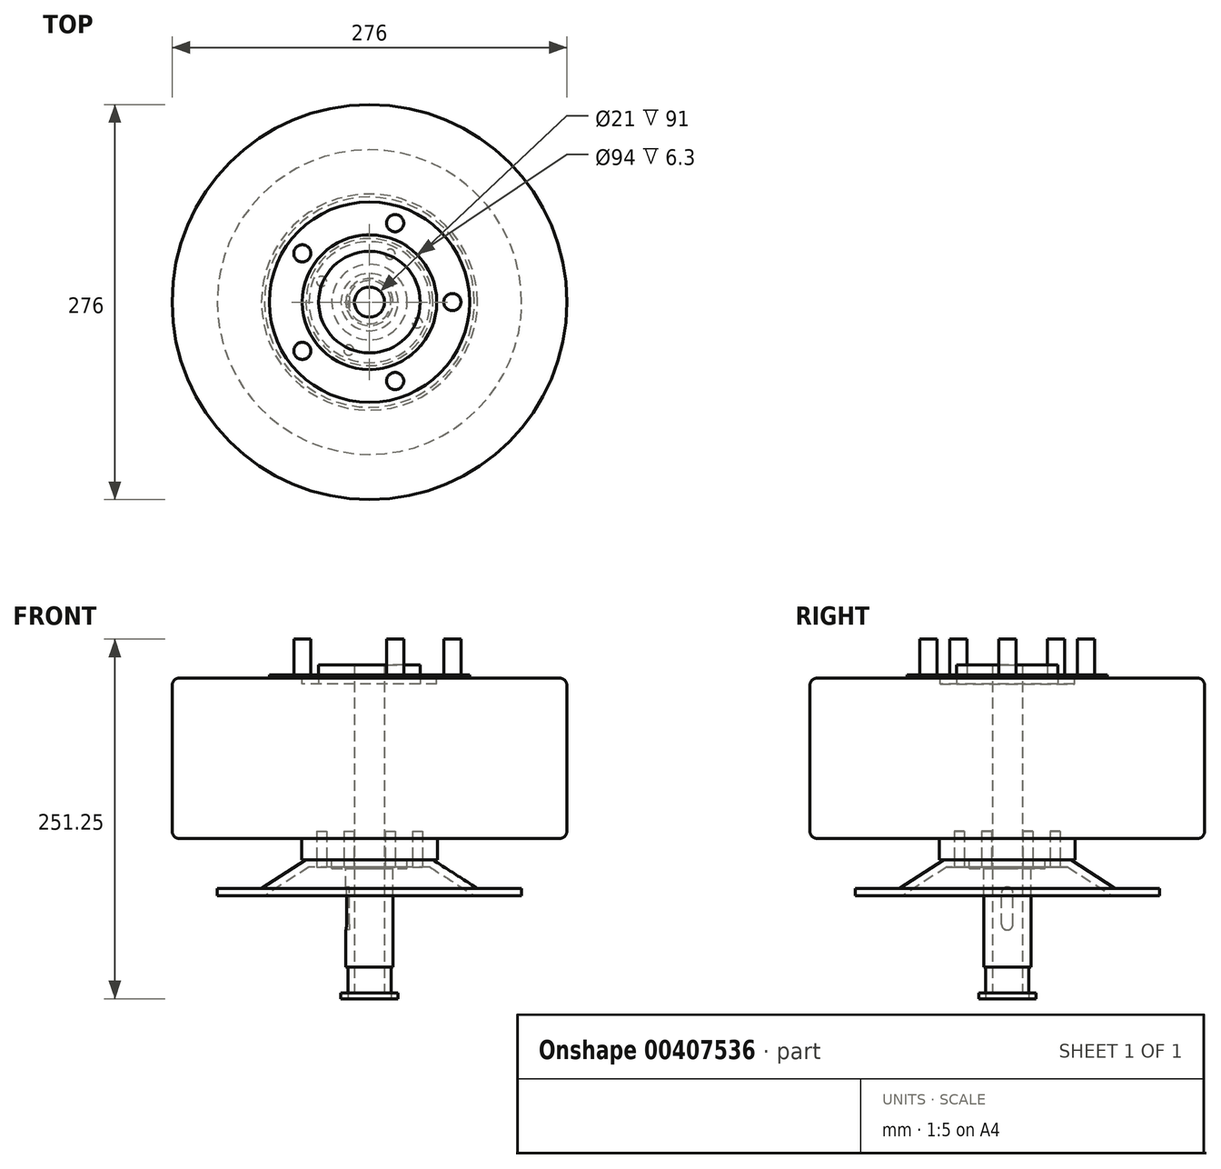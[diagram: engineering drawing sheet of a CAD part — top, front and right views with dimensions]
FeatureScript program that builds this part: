
annotation { "Feature Type Name" : "Feature", "Feature Type Description" : "" }
export const myFeature = defineFeature(function(context is Context, id is Id, definition is map)
    precondition{}
    {
        {
            var Q0;
            Q0=qCreatedBy(makeId("Top.planeOp"),FACE);
            var sketch = newSketch(context, id + "F0", { "sketchPlane" : qUnion([Q0])});
            skCircle(sketch, "E0", {"center": v(0, 0) * mm, "radius": 138 * mm});
            skSolve(sketch);
        }
        {
            var Q0;
            Q0=makeQuery(id+"F0.imprint","IMPRINT",FACE,{"disambiguationData":[TD([[makeQuery(id+"F0.imprint","IMPRINT",EDGE,{"derivedFrom":sQuery(id+"F0.wireOp",EDGE,"E0")}),1.0]])]});
            extrude(context, id + "F1", {"entities" : qUnion([Q0]), "depth" : 112 * mm, "offsetDistance" : 25.4 * mm});
        }
        {
            var Q0;
            Q0=makeQuery(id+"F1.opExtrude","CAP_FACE",FACE,{"disambiguationData":[OSD([sQuery(id+"F0.wireOp",EDGE,"E0")])],"isStart":false});
            var sketch = newSketch(context, id + "F2", { "sketchPlane" : qUnion([Q0])});
            skCircle(sketch, "E1", {"center": v(0, 0) * mm, "radius": 70 * mm});
            skSolve(sketch);
        }
        {
            var Q0;
            Q0 = qSketchRegion(id + "F2", true);
            extrude(context, id + "F3", {"entities" : qUnion([Q0]), "operationType" : NewBodyOperationType.ADD, "depth" : 2.25 * mm, "offsetDistance" : 25.4 * mm});
        }
        {
            var Q0;
            Q0=makeQuery(id+"F1.opExtrude","SWEPT_FACE",FACE,{"disambiguationData":[OSD([sQuery(id+"F0.wireOp",EDGE,"E0")])]});
            fillet(context, id + "F4", {"entities" : qUnion([Q0]), "tangentPropagation" : true, "radius" : 5 * mm, "defaultsChanged" : false, "vertexSettings" : [], "allowEdgeOverflow" : false});
        }
        {
            var Q0;
            Q0=makeQuery(id+"F3.opExtrude","CAP_FACE",FACE,{"disambiguationData":[OSD([sQuery(id+"F2.wireOp",EDGE,"E1")])],"isStart":false});
            var sketch = newSketch(context, id + "F5", { "sketchPlane" : qUnion([Q0])});
            skCircle(sketch, "E2", {"center": v(0, 0) * mm, "radius": 47 * mm});
            skSolve(sketch);
        }
        {
            var Q0;
            Q0 = qSketchRegion(id + "F5", true);
            extrude(context, id + "F6", {"entities" : qUnion([Q0]), "operationType" : NewBodyOperationType.REMOVE, "oppositeDirection" : true, "depth" : 6.3 * mm, "offsetDistance" : 25 * mm});
        }
        {
            var Q0;
            Q0=makeQuery(id+"F6.boolean.opBoolean","COPY",FACE,{"derivedFrom":makeQuery(id+"F6.opExtrude","CAP_FACE",FACE,{"disambiguationData":[OSD([sQuery(id+"F5.wireOp",EDGE,"E2")])],"isStart":false})});
            var sketch = newSketch(context, id + "F7", { "sketchPlane" : qUnion([Q0])});
            skCircle(sketch, "E3", {"center": v(0, 0) * mm, "radius": 35.5 * mm});
            skSolve(sketch);
        }
        {
            var Q0;
            Q0=makeQuery(id+"F3.opExtrude","CAP_FACE",FACE,{"disambiguationData":[OSD([sQuery(id+"F2.wireOp",EDGE,"E1")])],"isStart":false});
            var sketch = newSketch(context, id + "F8", { "sketchPlane" : qUnion([Q0])});
            skLineSegment(sketch, "E4", {"start": v(0, 0) * mm, "end": v(58, 0) * mm, "construction": true});
            skCircle(sketch, "E5", {"center": v(58, 0) * mm, "radius": 6 * mm});
            skCircle(sketch, "E6.1.0", {"center": v(17.92, 55.16) * mm, "radius": 6 * mm});
            skCircle(sketch, "E6.2.0", {"center": v(-46.92, 34.1) * mm, "radius": 6 * mm});
            skPoint(sketch, "E6.center", {"position": v(0, 0) * mm});
            skCircle(sketch, "E7.1.3.0", {"center": v(-46.92, -34.1) * mm, "radius": 6 * mm});
            skCircle(sketch, "E7.1.4.0", {"center": v(17.92, -55.16) * mm, "radius": 6 * mm});
            skSolve(sketch);
        }
        {
            var Q0;
            Q0 = qSketchRegion(id + "F8", true);
            extrude(context, id + "F9", {"entities" : qUnion([Q0]), "operationType" : NewBodyOperationType.ADD, "depth" : 25 * mm, "offsetDistance" : 25.4 * mm});
        }
        {
            var Q0;
            Q0 = qSketchRegion(id + "F7", true);
            extrude(context, id + "F10", {"entities" : qUnion([Q0]), "operationType" : NewBodyOperationType.ADD, "depth" : 13.3 * mm, "offsetDistance" : 25 * mm});
        }
        {
            var Q0;
            Q0=makeQuery(id+"F1.opExtrude","CAP_FACE",FACE,{"disambiguationData":[OSD([sQuery(id+"F0.wireOp",EDGE,"E0")])],"isStart":true});
            var sketch = newSketch(context, id + "F11", { "sketchPlane" : qUnion([Q0])});
            skCircle(sketch, "E8", {"center": v(0, 0) * mm, "radius": 47.5 * mm});
            skLineSegment(sketch, "E9", {"start": v(0, 0) * mm, "end": v(47.5, 0) * mm, "construction": true});
            skSolve(sketch);
        }
        {
            var Q0;
            Q0 = qSketchRegion(id + "F11", true);
            extrude(context, id + "F12", {"entities" : qUnion([Q0]), "operationType" : NewBodyOperationType.ADD, "depth" : 15 * mm, "offsetDistance" : 25 * mm});
        }
        {
            var Q0;
            Q0=makeQuery(id+"F12.opExtrude","CAP_FACE",FACE,{"disambiguationData":[OSD([sQuery(id+"F11.wireOp",EDGE,"E8")])],"isStart":false});
            var sketch = newSketch(context, id + "F13", { "sketchPlane" : qUnion([Q0])});
            skCircle(sketch, "E10", {"center": v(0, 0) * mm, "radius": 26.4 * mm});
            skLineSegment(sketch, "E11", {"start": v(0, 0) * mm, "end": v(26.4, 0) * mm, "construction": true});
            skSolve(sketch);
        }
        {
            var Q0;
            Q0 = qSketchRegion(id + "F13", true);
            extrude(context, id + "F14", {"entities" : qUnion([Q0]), "operationType" : NewBodyOperationType.ADD, "depth" : 6 * mm, "offsetDistance" : 25 * mm});
        }
        {
            var Q0;
            Q0=makeQuery(id+"F12.opExtrude","CAP_FACE",FACE,{"disambiguationData":[OSD([sQuery(id+"F11.wireOp",EDGE,"E8")])],"isStart":false});
            var sketch = newSketch(context, id + "F15", { "sketchPlane" : qUnion([Q0])});
            skCircle(sketch, "E12", {"center": v(33.5, 14.48) * mm, "radius": 3.5 * mm});
            skCircle(sketch, "E13.1.0", {"center": v(-14.48, 33.5) * mm, "radius": 3.5 * mm});
            skCircle(sketch, "E13.2.0", {"center": v(-33.5, -14.48) * mm, "radius": 3.5 * mm});
            skCircle(sketch, "E13.3.0", {"center": v(14.48, -33.5) * mm, "radius": 3.5 * mm});
            skPoint(sketch, "E13.center", {"position": v(0, 0) * mm});
            skSolve(sketch);
        }
        {
            var Q0;
            Q0 = qSketchRegion(id + "F15", true);
            extrude(context, id + "F16", {"entities" : qUnion([Q0]), "operationType" : NewBodyOperationType.REMOVE, "oppositeDirection" : true, "depth" : 12 * mm, "offsetDistance" : 25 * mm});
        }
        {
            var Q0;
            Q0=makeQuery(id+"F14.opExtrude","CAP_FACE",FACE,{"disambiguationData":[OSD([sQuery(id+"F13.wireOp",EDGE,"E10")])],"isStart":false});
            var sketch = newSketch(context, id + "F17", { "sketchPlane" : qUnion([Q0])});
            skCircle(sketch, "E14", {"center": v(0, 0) * mm, "radius": 16.5 * mm});
            skLineSegment(sketch, "E15", {"start": v(0, 0) * mm, "end": v(-16.5, 0) * mm, "construction": true});
            skSolve(sketch);
        }
        {
            var Q0;
            Q0 = qSketchRegion(id + "F17", true);
            extrude(context, id + "F18", {"entities" : qUnion([Q0]), "depth" : 69 * mm, "offsetDistance" : 25 * mm});
        }
        {
            var Q0;
            Q0=makeQuery(id+"F18.opExtrude","CAP_FACE",FACE,{"disambiguationData":[OSD([sQuery(id+"F17.wireOp",EDGE,"E14")])],"isStart":false});
            var sketch = newSketch(context, id + "F19", { "sketchPlane" : qUnion([Q0])});
            skCircle(sketch, "E16", {"center": v(0, 0) * mm, "radius": 15 * mm});
            skSolve(sketch);
        }
        {
            var Q0;
            Q0=makeQuery(id+"F19.imprint","IMPRINT",FACE,{"disambiguationData":[TD([[makeQuery(id+"F19.imprint","IMPRINT",EDGE,{"derivedFrom":sQuery(id+"F19.wireOp",EDGE,"E16")}),1.0]])]});
            extrude(context, id + "F20", {"entities" : qUnion([Q0]), "operationType" : NewBodyOperationType.ADD, "depth" : 22 * mm, "offsetDistance" : 25 * mm});
        }
        {
            var Q0;
            Q0=makeQuery(id+"F20.opExtrude","CAP_FACE",FACE,{"disambiguationData":[OSD([sQuery(id+"F19.wireOp",EDGE,"E16")])],"isStart":false});
            var sketch = newSketch(context, id + "F21", { "sketchPlane" : qUnion([Q0])});
            skCircle(sketch, "E17", {"center": v(0, 0) * mm, "radius": 10.5 * mm});
            skSolve(sketch);
        }
        {
            var Q0;
            Q0 = qSketchRegion(id + "F21", true);
            extrude(context, id + "F22", {"entities" : qUnion([Q0]), "operationType" : NewBodyOperationType.REMOVE, "endBound" : BoundingType.THROUGH_ALL, "oppositeDirection" : true, "depth" : 25 * mm, "offsetDistance" : 25 * mm});
        }
        {
            var Q0;
            Q0=makeQuery(id+"F18.opExtrude","CAP_FACE",FACE,{"disambiguationData":[OSD([sQuery(id+"F17.wireOp",EDGE,"E14")])],"isStart":true});
            var sketch = newSketch(context, id + "F23", { "sketchPlane" : qUnion([Q0])});
            skLineSegment(sketch, "E18", {"start": v(0, 0) * mm, "end": v(-16.5, 0) * mm});
            skSolve(sketch);
        }
        {
            var Q0;
            Q0=sQuery(id+"F23.wireOp",EDGE,"E18");
            var Q1;
            Q1=sQuery(id+"F23.wireOp",VERTEX,"E18.end");
            cPlane(context, id + "F24", {"entities" : qUnion([Q0, Q1]), "cplaneType" : CPlaneType.LINE_POINT, "offset" : 25 * mm, "width" : 150 * mm, "height" : 150 * mm});
        }
        {
            var Q0;
            Q0=qCreatedBy(id+"F24.planeOp",FACE);
            var sketch = newSketch(context, id + "F25", { "sketchPlane" : qUnion([Q0])});
            skLineSegment(sketch, "E19", {"start": v(4, -60) * mm, "end": v(4, -38) * mm});
            skLineSegment(sketch, "E20", {"start": v(-4, -60) * mm, "end": v(-4, -38) * mm});
            skArc(sketch, "E21", {"start": v(4, -60) * mm, "mid": v(0, -64) * mm, "end": v(-4, -60) * mm});
            skArc(sketch, "E22", {"start": v(-4, -38) * mm, "mid": v(0, -34) * mm, "end": v(4, -38) * mm});
            skSolve(sketch);
        }
        {
            var Q0;
            Q0 = qSketchRegion(id + "F25", true);
            extrude(context, id + "F26", {"entities" : qUnion([Q0]), "operationType" : NewBodyOperationType.REMOVE, "oppositeDirection" : true, "depth" : 2.6 * mm, "offsetDistance" : 25 * mm});
        }
        {
            var Q0;
            Q0=makeQuery(id+"F20.opExtrude","CAP_FACE",FACE,{"disambiguationData":[OSD([sQuery(id+"F19.wireOp",EDGE,"E16")])],"isStart":false});
            var sketch = newSketch(context, id + "F27", { "sketchPlane" : qUnion([Q0])});
            skCircle(sketch, "E23", {"center": v(0, 0) * mm, "radius": 20 * mm});
            skCircle(sketch, "E24", {"center": v(0, 0) * mm, "radius": 15 * mm});
            skSolve(sketch);
        }
        {
            var Q0;
            Q0 = qSketchRegion(id + "F27", true);
            extrude(context, id + "F28", {"entities" : qUnion([Q0]), "oppositeDirection" : true, "depth" : 4 * mm, "offsetDistance" : 25 * mm});
        }
        {
            var Q0;
            Q0=qCreatedBy(makeId("Front.planeOp"),FACE);
            var sketch = newSketch(context, id + "F29", { "sketchPlane" : qUnion([Q0])});
            skLineSegment(sketch, "E25", {"start": v(26.4, -15) * mm, "end": v(26.4, -20) * mm});
            skLineSegment(sketch, "E26", {"start": v(26.4, -15) * mm, "end": v(44.4, -15) * mm});
            skLineSegment(sketch, "E27", {"start": v(44.4, -15) * mm, "end": v(75.5, -35) * mm});
            skLineSegment(sketch, "E28", {"start": v(75.5, -35) * mm, "end": v(106.4, -35) * mm});
            skLineSegment(sketch, "E29", {"start": v(106.4, -35) * mm, "end": v(106.4, -40) * mm});
            skLineSegment(sketch, "E30", {"start": v(106.4, -40) * mm, "end": v(73.4, -40) * mm});
            skLineSegment(sketch, "E31", {"start": v(42.3, -20) * mm, "end": v(26.4, -20) * mm});
            skLineSegment(sketch, "E32", {"start": v(42.3, -20) * mm, "end": v(73.4, -40) * mm});
            skLineSegment(sketch, "E33", {"start": v(0, 0) * mm, "end": v(0, -75.4) * mm, "construction": true});
            skSolve(sketch);
        }
        {
            var Q0;
            Q0 = qSketchRegion(id + "F29", true);
            var Q1;
            Q1=sQuery(id+"F29.wireOp",EDGE,"E33");
            revolve(context, id + "F30", {"surfaceOperationType" : NewSurfaceOperationType.NEW, "entities" : qUnion([Q0]), "axis" : qUnion([Q1]), "revolveType" : RevolveType.FULL});
        }
        {
            var Q0;
            Q0=makeQuery(id+"F30.opRevolve","SWEPT_FACE",FACE,{"disambiguationData":[OSD([sQuery(id+"F29.wireOp",EDGE,"E31")])]});
            var sketch = newSketch(context, id + "F31", { "sketchPlane" : qUnion([Q0])});
            skCircle(sketch, "E34", {"center": v(33.5, 14.48) * mm, "radius": 3.5 * mm});
            skCircle(sketch, "E35.1.0", {"center": v(-14.48, 33.5) * mm, "radius": 3.5 * mm});
            skCircle(sketch, "E35.2.0", {"center": v(-33.5, -14.48) * mm, "radius": 3.5 * mm});
            skCircle(sketch, "E35.3.0", {"center": v(14.48, -33.5) * mm, "radius": 3.5 * mm});
            skPoint(sketch, "E35.center", {"position": v(0, 0) * mm});
            skSolve(sketch);
        }
        {
            var Q0;
            Q0 = qSketchRegion(id + "F31", true);
            extrude(context, id + "F32", {"entities" : qUnion([Q0]), "operationType" : NewBodyOperationType.REMOVE, "oppositeDirection" : true, "depth" : 25 * mm, "offsetDistance" : 25 * mm});
        }
    });
